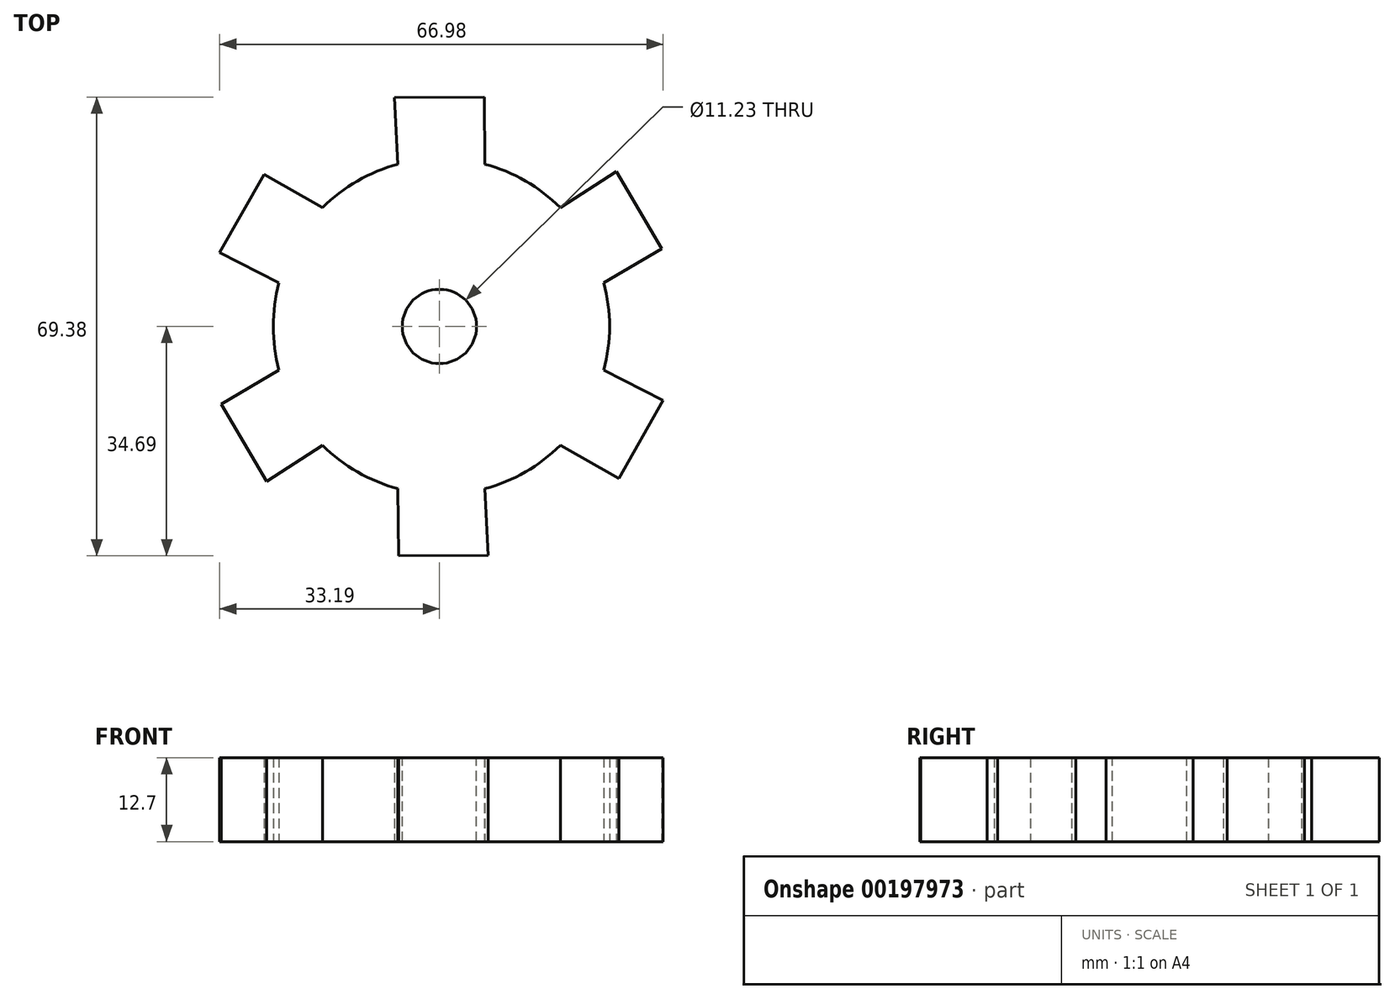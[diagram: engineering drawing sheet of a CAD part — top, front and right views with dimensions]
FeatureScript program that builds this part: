
annotation { "Feature Type Name" : "Feature", "Feature Type Description" : "" }
export const myFeature = defineFeature(function(context is Context, id is Id, definition is map)
    precondition{}
    {
        {
            var Q0;
            Q0=qCreatedBy(makeId("Top.planeOp"),FACE);
            var sketch = newSketch(context, id + "F0", { "sketchPlane" : qUnion([Q0])});
            skCircle(sketch, "E0", {"center": v(0, 0) * mm, "radius": 25.4 * mm});
            skSolve(sketch);
        }
        {
            var Q0;
            Q0=makeQuery(id+"F0.imprint","IMPRINT",FACE,{"disambiguationData":[TD([[makeQuery(id+"F0.imprint","IMPRINT",EDGE,{"derivedFrom":sQuery(id+"F0.wireOp",EDGE,"E0")}),1.0]])]});
            extrude(context, id + "F1", {"entities" : qUnion([Q0]), "endBound" : BoundingType.SYMMETRIC, "depth" : 12.7 * mm});
        }
        {
            var Q0;
            Q0=makeQuery(id+"F1.opExtrude","CAP_FACE",FACE,{"disambiguationData":[OSD([sQuery(id+"F0.wireOp",EDGE,"E0")])],"isStart":true});
            var sketch = newSketch(context, id + "F2", { "sketchPlane" : qUnion([Q0])});
            skLineSegment(sketch, "E1", {"start": v(0, 0) * mm, "end": v(0, 25.4) * mm});
            skLineSegment(sketch, "E2", {"start": v(0, 0) * mm, "end": v(6.57, 24.53) * mm});
            skLineSegment(sketch, "E3", {"start": v(-65.17, 34.88) * mm, "end": v(-65.68, 32.97) * mm});
            skLineSegment(sketch, "E4", {"start": v(0, 0) * mm, "end": v(-6.57, 24.53) * mm});
            skLineSegment(sketch, "E5", {"start": v(-6.57, 24.53) * mm, "end": v(7, 24.42) * mm});
            skLineSegment(sketch, "E6.0", {"start": v(-6.49, 34.7) * mm, "end": v(7.09, 34.58) * mm});
            skLineSegment(sketch, "E7", {"start": v(-6.49, 34.7) * mm, "end": v(-6.57, 24.53) * mm});
            skLineSegment(sketch, "E8", {"start": v(7.09, 34.58) * mm, "end": v(6.57, 24.53) * mm});
            skSolve(sketch);
        }
        {
            var Q0;
            {var subQ0=sQuery(id+"F2.wireOp",EDGE,"E1");var subQ1=makeQuery(id+"F1.opExtrude","CAP_EDGE",EDGE,{"disambiguationData":[OSD([sQuery(id+"F0.wireOp",EDGE,"E0")])],"isStart":true});var subQ2=makeQuery(id+"F2.imprint","INTERSECT",VERTEX,{"derivedFrom":[subQ1,subQ0]});Q0=makeQuery(id+"F2.imprint","IMPRINT",FACE,{"disambiguationData":[TD([[makeQuery(id+"F2.imprint","IMPRINT",EDGE,{"disambiguationData":[TD([[subQ2,1.0]])],"derivedFrom":subQ0}),1.0]])]});}
            var Q1;
            {var subQ1=makeQuery(id+"F1.opExtrude","CAP_EDGE",EDGE,{"disambiguationData":[OSD([sQuery(id+"F0.wireOp",EDGE,"E0")])],"isStart":true});var subQ5=sQuery(id+"F2.wireOp",EDGE,"E1");var subQ6=makeQuery(id+"F2.imprint","INTERSECT",VERTEX,{"derivedFrom":[subQ1,subQ5]});Q1=makeQuery(id+"F2.imprint","IMPRINT",FACE,{"disambiguationData":[TD([[makeQuery(id+"F2.imprint","IMPRINT",EDGE,{"disambiguationData":[TD([[subQ6,1.0]])],"derivedFrom":subQ5}),-1.0]])]});}
            var Q2;
            {var subQ0=sQuery(id+"F2.wireOp",EDGE,"E1");var subQ1=makeQuery(id+"F1.opExtrude","CAP_EDGE",EDGE,{"disambiguationData":[OSD([sQuery(id+"F0.wireOp",EDGE,"E0")])],"isStart":true});var subQ2=makeQuery(id+"F2.imprint","INTERSECT",VERTEX,{"derivedFrom":[subQ1,subQ0]});Q2=makeQuery(id+"F2.imprint","IMPRINT",FACE,{"disambiguationData":[TD([[makeQuery(id+"F2.imprint","IMPRINT",EDGE,{"disambiguationData":[TD([[subQ2,1.0]])],"derivedFrom":subQ0}),1.0]])]});}
            var Q3;
            {var subQ1=makeQuery(id+"F1.opExtrude","CAP_EDGE",EDGE,{"disambiguationData":[OSD([sQuery(id+"F0.wireOp",EDGE,"E0")])],"isStart":true});var subQ5=sQuery(id+"F2.wireOp",EDGE,"E1");var subQ6=makeQuery(id+"F2.imprint","INTERSECT",VERTEX,{"derivedFrom":[subQ1,subQ5]});Q3=makeQuery(id+"F2.imprint","IMPRINT",FACE,{"disambiguationData":[TD([[makeQuery(id+"F2.imprint","IMPRINT",EDGE,{"disambiguationData":[TD([[subQ6,1.0]])],"derivedFrom":subQ5}),-1.0]])]});}
            var Q4;
            Q4=makeQuery(id+"F2.imprint","IMPRINT",FACE,{"disambiguationData":[TD([[makeQuery(id+"F2.imprint","IMPRINT",EDGE,{"derivedFrom":sQuery(id+"F2.wireOp",EDGE,"E6.0")}),-1.0]])]});
            extrude(context, id + "F3", {"entities" : qUnion([Q0, Q1, Q2, Q3, Q4]), "operationType" : NewBodyOperationType.ADD, "oppositeDirection" : true, "depth" : 12.7 * mm});
        }
        {
            var Q0;
            Q0=qCreatedBy(makeId("Front.planeOp"),FACE);
            var sketch = newSketch(context, id + "F4", { "sketchPlane" : qUnion([Q0])});
            skLineSegment(sketch, "E9", {"start": v(0, 0) * mm, "end": v(0, 44.48) * mm});
            skSolve(sketch);
        }
        {
            var Q0;
            Q0=makeQuery(id+"F1.opExtrude","SWEPT_BODY",BODY,{"disambiguationData":[OSD([sQuery(id+"F0.wireOp",EDGE,"E0")])]});
            var Q1;
            Q1=sQuery(id+"F4.wireOp",EDGE,"E9");
            circularPattern(context, id + "F5", {"operationType" : NewBodyOperationType.ADD, "entities" : qUnion([Q0]), "axis" : qUnion([Q1]), "angle" : 360 * degree, "instanceCount" : 6, "equalSpace" : true});
        }
        {
            var Q0;
            {var subQ0=makeQuery(id+"F3.boolean.opBoolean","MERGE",FACE,{"derivedFrom":[makeQuery(id+"F1.opExtrude","CAP_FACE",FACE,{"disambiguationData":[OSD([sQuery(id+"F0.wireOp",EDGE,"E0")])],"isStart":false}),makeQuery(id+"F3.opExtrude","CAP_FACE",FACE,{"disambiguationData":[OSD([sQuery(id+"F2.wireOp",EDGE,"E2"),sQuery(id+"F2.wireOp",EDGE,"E5"),sQuery(id+"F2.wireOp",EDGE,"E6.0"),sQuery(id+"F2.wireOp",EDGE,"E7"),sQuery(id+"F2.wireOp",EDGE,"E8")])],"isStart":false})]});Q0=makeQuery(id+"F5.boolean.opBoolean","MERGE",FACE,{"derivedFrom":[subQ0,makeQuery(id+"F5.opPattern","COPY",FACE,{"derivedFrom":subQ0,"instanceName":"1"}),makeQuery(id+"F5.opPattern","COPY",FACE,{"derivedFrom":subQ0,"instanceName":"2"}),makeQuery(id+"F5.opPattern","COPY",FACE,{"derivedFrom":subQ0,"instanceName":"3"}),makeQuery(id+"F5.opPattern","COPY",FACE,{"derivedFrom":subQ0,"instanceName":"4"}),makeQuery(id+"F5.opPattern","COPY",FACE,{"derivedFrom":subQ0,"instanceName":"5"})]});}
            var sketch = newSketch(context, id + "F6", { "sketchPlane" : qUnion([Q0])});
            skCircle(sketch, "E10", {"center": v(-0.3, 0) * mm, "radius": 5.62 * mm});
            skPoint(sketch, "E10.centerSnap0", {"position": v(-0.3, 34.64) * mm});
            skSolve(sketch);
        }
        {
            var Q0;
            Q0=makeQuery(id+"F6.imprint","IMPRINT",FACE,{"disambiguationData":[TD([[makeQuery(id+"F6.imprint","IMPRINT",EDGE,{"derivedFrom":sQuery(id+"F6.wireOp",EDGE,"E10")}),1.0]])]});
            extrude(context, id + "F7", {"entities" : qUnion([Q0]), "operationType" : NewBodyOperationType.REMOVE, "oppositeDirection" : true, "depth" : 12.7 * mm});
        }
    });
